# Revit family: BTALU560
name_source: partatom
category: Structural Connections
revit_build: Autodesk Revit 2014 (Build: 20130308_1515(x64)
units: mm (PartAtom-declared; Revit-internal decimal feet)

## types (1)
- BTALU560
    Default Elevation = 0 mm  [stored 0 ft]
    Density = 1.43 kg
    Description = Concealed beam hanger
    EPD = https://www.strongtie.eu
    ETA / DoP = https://www.strongtie.eu
    Manufacturer = Simpson Strong-Tie
    Model = BTALU560
    Model Disclaimer = Contact Simpson Strong-Tie Company  for more information
    Model ID = 0240693464240618745400879047176084736236
    Name = BTALU560
    ObjectType = BTALU560
    Product Material = Aluminium
    Product Type = Concealed beam hanger
    Reference = BTALU560
    Technical datasheet = https://www.strongtie.eu
    URL = www.strongtie.eu
    UniClass Number = Pr_20_29_31_13
    UniClass Title = Carbon steel punched metal plate fasteners

note: [stored X ft] marks values corroborated as IEEE doubles in the binary element streams (Revit-internal decimal feet)

## geometry (parser evidence)
native form markers: Blend x33, Sweep x1
no freeform markers — native parametric forms only
